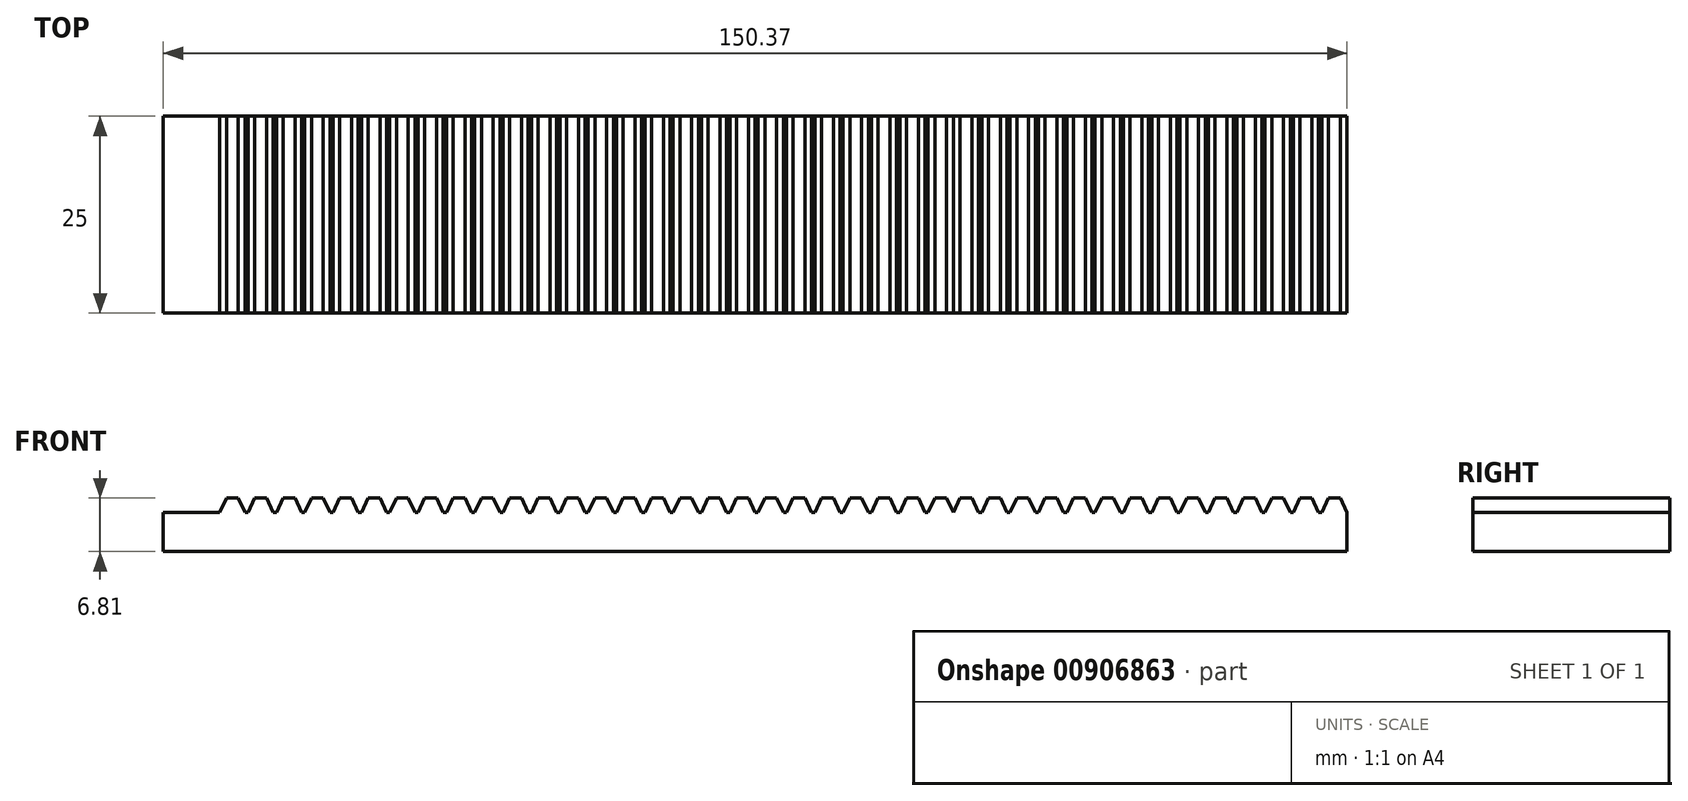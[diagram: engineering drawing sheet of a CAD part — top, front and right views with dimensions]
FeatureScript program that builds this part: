
annotation { "Feature Type Name" : "Feature", "Feature Type Description" : "" }
export const myFeature = defineFeature(function(context is Context, id is Id, definition is map)
    precondition{}
    {
        {
            var Q0;
            Q0=qCreatedBy(makeId("Front.planeOp"),FACE);
            var sketch = newSketch(context, id + "F0", { "sketchPlane" : qUnion([Q0])});
            skLineSegment(sketch, "E0.bottom", {"start": v(0, 5) * mm, "end": v(49.96, 5) * mm});
            skLineSegment(sketch, "E0.top", {"start": v(0, 0) * mm, "end": v(49.96, 0) * mm});
            skLineSegment(sketch, "E1", {"start": v(-4.28, 8.32) * mm, "end": v(-4.28, 8.32) * mm});
            skLineSegment(sketch, "E2", {"start": v(21.59, 5) * mm, "end": v(22.43, 6.81) * mm});
            skLineSegment(sketch, "E3", {"start": v(22.43, 6.81) * mm, "end": v(23.93, 6.81) * mm});
            skLineSegment(sketch, "E4", {"start": v(23.93, 6.81) * mm, "end": v(24.78, 5) * mm});
            skLineSegment(sketch, "E5", {"start": v(-1.09, 8.32) * mm, "end": v(-1.09, 8.32) * mm});
            skLineSegment(sketch, "E6", {"start": v(23.93, 6.81) * mm, "end": v(23.93, -3.78) * mm, "construction": true});
            skLineSegment(sketch, "E7", {"start": v(22.43, 6.81) * mm, "end": v(22.43, -3.82) * mm, "construction": true});
            skLineSegment(sketch, "E8.MirrorCS", {"start": v(26.03, 6.81) * mm, "end": v(25.19, 5) * mm});
            skLineSegment(sketch, "E9.MirrorCS", {"start": v(-0.68, 8.32) * mm, "end": v(-0.68, 8.32) * mm});
            skLineSegment(sketch, "E10.MirrorCS", {"start": v(2.51, 8.32) * mm, "end": v(2.51, 8.32) * mm});
            skLineSegment(sketch, "E11.MirrorCS", {"start": v(27.53, 6.81) * mm, "end": v(26.03, 6.81) * mm});
            skLineSegment(sketch, "E12.MirrorCS", {"start": v(28.38, 5) * mm, "end": v(27.53, 6.81) * mm});
            skLineSegment(sketch, "E13.1.0.0", {"start": v(31.13, 6.81) * mm, "end": v(31.97, 5) * mm});
            skLineSegment(sketch, "E13.1.0.1", {"start": v(28.78, 5) * mm, "end": v(29.63, 6.81) * mm});
            skLineSegment(sketch, "E13.1.0.2", {"start": v(33.23, 6.81) * mm, "end": v(32.38, 5) * mm});
            skLineSegment(sketch, "E13.1.0.3", {"start": v(34.73, 6.81) * mm, "end": v(33.23, 6.81) * mm});
            skLineSegment(sketch, "E13.1.0.4", {"start": v(35.57, 5) * mm, "end": v(34.73, 6.81) * mm});
            skLineSegment(sketch, "E13.1.0.5", {"start": v(29.63, 6.81) * mm, "end": v(31.13, 6.81) * mm});
            skLineSegment(sketch, "E13.2.0.0", {"start": v(38.33, 6.81) * mm, "end": v(39.17, 5) * mm});
            skLineSegment(sketch, "E13.2.0.1", {"start": v(35.98, 5) * mm, "end": v(36.83, 6.81) * mm});
            skLineSegment(sketch, "E13.2.0.5", {"start": v(36.83, 6.81) * mm, "end": v(38.33, 6.81) * mm});
            skLineSegment(sketch, "E13.direction1", {"start": v(21.59, 5) * mm, "end": v(28.78, 5) * mm, "construction": true});
            skLineSegment(sketch, "E14", {"start": v(10.8, 5) * mm, "end": v(11.64, 6.81) * mm});
            skLineSegment(sketch, "E15", {"start": v(11.64, 6.81) * mm, "end": v(13.14, 6.81) * mm});
            skLineSegment(sketch, "E16", {"start": v(13.14, 6.81) * mm, "end": v(13.98, 5) * mm});
            skLineSegment(sketch, "E17", {"start": v(17.99, 5) * mm, "end": v(18.84, 6.81) * mm});
            skLineSegment(sketch, "E18", {"start": v(18.84, 6.81) * mm, "end": v(20.34, 6.81) * mm});
            skLineSegment(sketch, "E19", {"start": v(20.34, 6.81) * mm, "end": v(21.18, 5) * mm});
            skLineSegment(sketch, "E20", {"start": v(14.4, 5) * mm, "end": v(15.24, 6.81) * mm});
            skLineSegment(sketch, "E21", {"start": v(15.24, 6.81) * mm, "end": v(16.74, 6.81) * mm});
            skLineSegment(sketch, "E22", {"start": v(16.74, 6.81) * mm, "end": v(17.58, 5) * mm});
            skLineSegment(sketch, "E23", {"start": v(-4.21, 6.19) * mm, "end": v(53.42, 6.19) * mm, "construction": true});
            skPoint(sketch, "E24", {"position": v(27.82, 6.19) * mm});
            skLineSegment(sketch, "E25", {"start": v(7.2, 5) * mm, "end": v(8.04, 6.81) * mm});
            skLineSegment(sketch, "E26", {"start": v(8.04, 6.81) * mm, "end": v(9.54, 6.81) * mm});
            skLineSegment(sketch, "E27", {"start": v(9.54, 6.81) * mm, "end": v(10.39, 5) * mm});
            skLineSegment(sketch, "E28", {"start": v(3.6, 5) * mm, "end": v(4.44, 6.81) * mm});
            skLineSegment(sketch, "E29", {"start": v(4.44, 6.81) * mm, "end": v(5.94, 6.81) * mm});
            skLineSegment(sketch, "E30", {"start": v(5.94, 6.81) * mm, "end": v(6.79, 5) * mm});
            skLineSegment(sketch, "E31", {"start": v(0, 5) * mm, "end": v(0.85, 6.81) * mm});
            skLineSegment(sketch, "E32", {"start": v(0.85, 6.81) * mm, "end": v(2.35, 6.81) * mm});
            skLineSegment(sketch, "E33", {"start": v(2.35, 6.81) * mm, "end": v(3.2, 5) * mm});
            skLineSegment(sketch, "E34", {"start": v(17.86, 9.76) * mm, "end": v(17.86, 9.76) * mm});
            skLineSegment(sketch, "E35", {"start": v(43.18, 5) * mm, "end": v(44.02, 6.81) * mm});
            skLineSegment(sketch, "E36", {"start": v(44.02, 6.81) * mm, "end": v(45.52, 6.81) * mm});
            skLineSegment(sketch, "E37", {"start": v(45.52, 6.81) * mm, "end": v(46.37, 5) * mm});
            skLineSegment(sketch, "E38", {"start": v(46.77, 5) * mm, "end": v(47.62, 6.81) * mm});
            skLineSegment(sketch, "E39", {"start": v(47.62, 6.81) * mm, "end": v(49.12, 6.81) * mm});
            skLineSegment(sketch, "E40", {"start": v(49.12, 6.81) * mm, "end": v(49.96, 5) * mm});
            skLineSegment(sketch, "E41", {"start": v(16.5, 8.14) * mm, "end": v(16.5, 8.14) * mm});
            skLineSegment(sketch, "E42", {"start": v(39.58, 5) * mm, "end": v(40.42, 6.81) * mm});
            skLineSegment(sketch, "E43", {"start": v(40.42, 6.81) * mm, "end": v(41.92, 6.81) * mm});
            skLineSegment(sketch, "E44", {"start": v(41.92, 6.81) * mm, "end": v(42.77, 5) * mm});
            skLineSegment(sketch, "E45", {"start": v(19.69, 8.14) * mm, "end": v(19.69, 8.14) * mm});
            skLineSegment(sketch, "E46", {"start": v(0, 5) * mm, "end": v(0, 0) * mm});
            skPoint(sketch, "E47.orphan", {"position": v(0, -0.17) * mm});
            skLineSegment(sketch, "E48", {"start": v(49.96, 5) * mm, "end": v(50.37, 5) * mm});
            skLineSegment(sketch, "E49", {"start": v(50.37, 0) * mm, "end": v(49.96, 0) * mm});
            skLineSegment(sketch, "E50.bottom", {"start": v(50.37, 5) * mm, "end": v(100.37, 5) * mm});
            skLineSegment(sketch, "E50.top", {"start": v(50.37, 0) * mm, "end": v(100.37, 0) * mm});
            skLineSegment(sketch, "E51", {"start": v(20.56, -3.86) * mm, "end": v(20.56, -3.86) * mm});
            skLineSegment(sketch, "E52", {"start": v(71.98, 5) * mm, "end": v(72.82, 6.81) * mm});
            skLineSegment(sketch, "E53", {"start": v(72.82, 6.81) * mm, "end": v(74.32, 6.81) * mm});
            skLineSegment(sketch, "E54", {"start": v(74.32, 6.81) * mm, "end": v(75.17, 5) * mm});
            skLineSegment(sketch, "E55", {"start": v(23.75, -3.86) * mm, "end": v(23.75, -3.86) * mm});
            skLineSegment(sketch, "E56", {"start": v(74.32, 6.81) * mm, "end": v(74.32, -3.78) * mm, "construction": true});
            skLineSegment(sketch, "E57", {"start": v(72.82, 6.81) * mm, "end": v(72.82, -3.82) * mm, "construction": true});
            skLineSegment(sketch, "E58.MirrorCS", {"start": v(76.42, 6.81) * mm, "end": v(75.58, 5) * mm});
            skLineSegment(sketch, "E59.MirrorCS", {"start": v(24.16, -3.86) * mm, "end": v(24.16, -3.86) * mm});
            skLineSegment(sketch, "E60.MirrorCS", {"start": v(27.35, -3.86) * mm, "end": v(27.35, -3.86) * mm});
            skLineSegment(sketch, "E61.MirrorCS", {"start": v(77.92, 6.81) * mm, "end": v(76.42, 6.81) * mm});
            skLineSegment(sketch, "E62.MirrorCS", {"start": v(78.77, 5) * mm, "end": v(77.92, 6.81) * mm});
            skLineSegment(sketch, "E63", {"start": v(50.22, 5) * mm, "end": v(100.66, 5) * mm, "construction": true});
            skLineSegment(sketch, "E64.1.0.0", {"start": v(81.52, 6.81) * mm, "end": v(82.36, 5) * mm});
            skLineSegment(sketch, "E64.1.0.1", {"start": v(79.17, 5) * mm, "end": v(80.02, 6.81) * mm});
            skLineSegment(sketch, "E64.1.0.2", {"start": v(83.62, 6.81) * mm, "end": v(82.77, 5) * mm});
            skLineSegment(sketch, "E64.1.0.3", {"start": v(85.12, 6.81) * mm, "end": v(83.62, 6.81) * mm});
            skLineSegment(sketch, "E64.1.0.4", {"start": v(85.96, 5) * mm, "end": v(85.12, 6.81) * mm});
            skLineSegment(sketch, "E64.1.0.5", {"start": v(80.02, 6.81) * mm, "end": v(81.52, 6.81) * mm});
            skLineSegment(sketch, "E64.2.0.0", {"start": v(88.71, 6.81) * mm, "end": v(89.56, 5) * mm});
            skLineSegment(sketch, "E64.2.0.1", {"start": v(86.37, 5) * mm, "end": v(87.21, 6.81) * mm});
            skLineSegment(sketch, "E64.2.0.5", {"start": v(87.21, 6.81) * mm, "end": v(88.71, 6.81) * mm});
            skLineSegment(sketch, "E64.direction1", {"start": v(71.98, 5) * mm, "end": v(79.17, 5) * mm, "construction": true});
            skLineSegment(sketch, "E65", {"start": v(61.18, 5) * mm, "end": v(62.03, 6.81) * mm});
            skLineSegment(sketch, "E66", {"start": v(62.03, 6.81) * mm, "end": v(63.53, 6.81) * mm});
            skLineSegment(sketch, "E67", {"start": v(63.53, 6.81) * mm, "end": v(64.37, 5) * mm});
            skLineSegment(sketch, "E68", {"start": v(68.38, 5) * mm, "end": v(69.22, 6.81) * mm});
            skLineSegment(sketch, "E69", {"start": v(69.22, 6.81) * mm, "end": v(70.72, 6.81) * mm});
            skLineSegment(sketch, "E70", {"start": v(70.72, 6.81) * mm, "end": v(71.57, 5) * mm});
            skLineSegment(sketch, "E71", {"start": v(64.78, 5) * mm, "end": v(65.63, 6.81) * mm});
            skLineSegment(sketch, "E72", {"start": v(65.63, 6.81) * mm, "end": v(67.13, 6.81) * mm});
            skLineSegment(sketch, "E73", {"start": v(67.13, 6.81) * mm, "end": v(67.97, 5) * mm});
            skLineSegment(sketch, "E74", {"start": v(46.18, 6.19) * mm, "end": v(103.81, 6.19) * mm, "construction": true});
            skPoint(sketch, "E75", {"position": v(78.21, 6.19) * mm});
            skLineSegment(sketch, "E76", {"start": v(57.59, 5) * mm, "end": v(58.43, 6.81) * mm});
            skLineSegment(sketch, "E77", {"start": v(58.43, 6.81) * mm, "end": v(59.93, 6.81) * mm});
            skLineSegment(sketch, "E78", {"start": v(59.93, 6.81) * mm, "end": v(60.78, 5) * mm});
            skLineSegment(sketch, "E79", {"start": v(53.99, 5) * mm, "end": v(54.83, 6.81) * mm});
            skLineSegment(sketch, "E80", {"start": v(54.83, 6.81) * mm, "end": v(56.33, 6.81) * mm});
            skLineSegment(sketch, "E81", {"start": v(56.33, 6.81) * mm, "end": v(57.18, 5) * mm});
            skLineSegment(sketch, "E82", {"start": v(50.39, 5) * mm, "end": v(51.23, 6.81) * mm});
            skLineSegment(sketch, "E83", {"start": v(51.23, 6.81) * mm, "end": v(52.73, 6.81) * mm});
            skLineSegment(sketch, "E84", {"start": v(52.73, 6.81) * mm, "end": v(53.58, 5) * mm});
            skLineSegment(sketch, "E85", {"start": v(42.7, -2.42) * mm, "end": v(42.7, -2.42) * mm});
            skLineSegment(sketch, "E86", {"start": v(93.57, 5) * mm, "end": v(94.41, 6.81) * mm});
            skLineSegment(sketch, "E87", {"start": v(94.41, 6.81) * mm, "end": v(95.91, 6.81) * mm});
            skLineSegment(sketch, "E88", {"start": v(95.91, 6.81) * mm, "end": v(96.76, 5) * mm});
            skLineSegment(sketch, "E89", {"start": v(97.16, 5) * mm, "end": v(98, 6.81) * mm});
            skLineSegment(sketch, "E90", {"start": v(98, 6.81) * mm, "end": v(99.5, 6.81) * mm});
            skLineSegment(sketch, "E91", {"start": v(99.5, 6.81) * mm, "end": v(100.35, 5) * mm});
            skLineSegment(sketch, "E92", {"start": v(41.33, -4.04) * mm, "end": v(41.33, -4.04) * mm});
            skLineSegment(sketch, "E93", {"start": v(89.97, 5) * mm, "end": v(90.81, 6.81) * mm});
            skLineSegment(sketch, "E94", {"start": v(90.81, 6.81) * mm, "end": v(92.31, 6.81) * mm});
            skLineSegment(sketch, "E95", {"start": v(92.31, 6.81) * mm, "end": v(93.16, 5) * mm});
            skLineSegment(sketch, "E96", {"start": v(44.52, -4.04) * mm, "end": v(44.52, -4.04) * mm});
            skLineSegment(sketch, "E97.bottom", {"start": v(100.37, 5) * mm, "end": v(150.37, 5) * mm});
            skLineSegment(sketch, "E97.top", {"start": v(100.37, 0) * mm, "end": v(150.37, 0) * mm});
            skLineSegment(sketch, "E97.right", {"start": v(150.37, 5) * mm, "end": v(150.37, 0) * mm});
            skLineSegment(sketch, "E98", {"start": v(120.1, 1.73) * mm, "end": v(120.1, 1.73) * mm});
            skLineSegment(sketch, "E99", {"start": v(121.98, 5) * mm, "end": v(122.82, 6.81) * mm});
            skLineSegment(sketch, "E100", {"start": v(122.82, 6.81) * mm, "end": v(124.32, 6.81) * mm});
            skLineSegment(sketch, "E101", {"start": v(124.32, 6.81) * mm, "end": v(125.17, 5) * mm});
            skLineSegment(sketch, "E102", {"start": v(123.3, 1.73) * mm, "end": v(123.3, 1.73) * mm});
            skLineSegment(sketch, "E103", {"start": v(124.32, 6.81) * mm, "end": v(124.32, -3.78) * mm, "construction": true});
            skLineSegment(sketch, "E104", {"start": v(122.82, 6.81) * mm, "end": v(122.82, -3.82) * mm, "construction": true});
            skLineSegment(sketch, "E105.MirrorCS", {"start": v(126.42, 6.81) * mm, "end": v(125.58, 5) * mm});
            skLineSegment(sketch, "E106.MirrorCS", {"start": v(123.7, 1.73) * mm, "end": v(123.7, 1.73) * mm});
            skLineSegment(sketch, "E107.MirrorCS", {"start": v(126.9, 1.73) * mm, "end": v(126.9, 1.73) * mm});
            skLineSegment(sketch, "E108.MirrorCS", {"start": v(127.92, 6.81) * mm, "end": v(126.42, 6.81) * mm});
            skLineSegment(sketch, "E109.MirrorCS", {"start": v(128.77, 5) * mm, "end": v(127.92, 6.81) * mm});
            skLineSegment(sketch, "E110", {"start": v(100.22, 5) * mm, "end": v(150.66, 5) * mm, "construction": true});
            skLineSegment(sketch, "E111.1.0.0", {"start": v(131.52, 6.81) * mm, "end": v(132.36, 5) * mm});
            skLineSegment(sketch, "E111.1.0.1", {"start": v(129.17, 5) * mm, "end": v(130.02, 6.81) * mm});
            skLineSegment(sketch, "E111.1.0.2", {"start": v(133.62, 6.81) * mm, "end": v(132.77, 5) * mm});
            skLineSegment(sketch, "E111.1.0.3", {"start": v(135.12, 6.81) * mm, "end": v(133.62, 6.81) * mm});
            skLineSegment(sketch, "E111.1.0.4", {"start": v(135.96, 5) * mm, "end": v(135.12, 6.81) * mm});
            skLineSegment(sketch, "E111.1.0.5", {"start": v(130.02, 6.81) * mm, "end": v(131.52, 6.81) * mm});
            skLineSegment(sketch, "E111.2.0.0", {"start": v(138.71, 6.81) * mm, "end": v(139.56, 5) * mm});
            skLineSegment(sketch, "E111.2.0.1", {"start": v(136.37, 5) * mm, "end": v(137.21, 6.81) * mm});
            skLineSegment(sketch, "E111.2.0.5", {"start": v(137.21, 6.81) * mm, "end": v(138.71, 6.81) * mm});
            skLineSegment(sketch, "E111.direction1", {"start": v(121.98, 5) * mm, "end": v(129.17, 5) * mm, "construction": true});
            skLineSegment(sketch, "E112", {"start": v(111.18, 5) * mm, "end": v(112.03, 6.81) * mm});
            skLineSegment(sketch, "E113", {"start": v(112.03, 6.81) * mm, "end": v(113.53, 6.81) * mm});
            skLineSegment(sketch, "E114", {"start": v(113.53, 6.81) * mm, "end": v(114.37, 5) * mm});
            skLineSegment(sketch, "E115", {"start": v(118.38, 5) * mm, "end": v(119.22, 6.81) * mm});
            skLineSegment(sketch, "E116", {"start": v(119.22, 6.81) * mm, "end": v(120.72, 6.81) * mm});
            skLineSegment(sketch, "E117", {"start": v(120.72, 6.81) * mm, "end": v(121.57, 5) * mm});
            skLineSegment(sketch, "E118", {"start": v(114.78, 5) * mm, "end": v(115.63, 6.81) * mm});
            skLineSegment(sketch, "E119", {"start": v(115.63, 6.81) * mm, "end": v(117.13, 6.81) * mm});
            skLineSegment(sketch, "E120", {"start": v(117.13, 6.81) * mm, "end": v(117.97, 5) * mm});
            skLineSegment(sketch, "E121", {"start": v(96.18, 6.19) * mm, "end": v(153.81, 6.19) * mm, "construction": true});
            skPoint(sketch, "E122", {"position": v(128.21, 6.19) * mm});
            skLineSegment(sketch, "E123", {"start": v(107.59, 5) * mm, "end": v(108.43, 6.81) * mm});
            skLineSegment(sketch, "E124", {"start": v(108.43, 6.81) * mm, "end": v(109.93, 6.81) * mm});
            skLineSegment(sketch, "E125", {"start": v(109.93, 6.81) * mm, "end": v(110.78, 5) * mm});
            skLineSegment(sketch, "E126", {"start": v(103.99, 5) * mm, "end": v(104.83, 6.81) * mm});
            skLineSegment(sketch, "E127", {"start": v(104.83, 6.81) * mm, "end": v(106.33, 6.81) * mm});
            skLineSegment(sketch, "E128", {"start": v(106.33, 6.81) * mm, "end": v(107.18, 5) * mm});
            skLineSegment(sketch, "E129", {"start": v(100.39, 5) * mm, "end": v(101.23, 6.81) * mm});
            skLineSegment(sketch, "E130", {"start": v(101.23, 6.81) * mm, "end": v(102.73, 6.81) * mm});
            skLineSegment(sketch, "E131", {"start": v(102.73, 6.81) * mm, "end": v(103.58, 5) * mm});
            skLineSegment(sketch, "E132", {"start": v(142.24, 3.17) * mm, "end": v(142.24, 3.17) * mm});
            skLineSegment(sketch, "E133", {"start": v(143.57, 5) * mm, "end": v(144.41, 6.81) * mm});
            skLineSegment(sketch, "E134", {"start": v(144.41, 6.81) * mm, "end": v(145.91, 6.81) * mm});
            skLineSegment(sketch, "E135", {"start": v(145.91, 6.81) * mm, "end": v(146.76, 5) * mm});
            skLineSegment(sketch, "E136", {"start": v(147.16, 5) * mm, "end": v(148, 6.81) * mm});
            skLineSegment(sketch, "E137", {"start": v(148, 6.81) * mm, "end": v(149.5, 6.81) * mm});
            skLineSegment(sketch, "E138", {"start": v(149.5, 6.81) * mm, "end": v(150.35, 5) * mm});
            skLineSegment(sketch, "E139", {"start": v(140.88, 1.56) * mm, "end": v(140.88, 1.56) * mm});
            skLineSegment(sketch, "E140", {"start": v(139.97, 5) * mm, "end": v(140.81, 6.81) * mm});
            skLineSegment(sketch, "E141", {"start": v(140.81, 6.81) * mm, "end": v(142.31, 6.81) * mm});
            skLineSegment(sketch, "E142", {"start": v(142.31, 6.81) * mm, "end": v(143.16, 5) * mm});
            skLineSegment(sketch, "E143", {"start": v(144.07, 1.56) * mm, "end": v(144.07, 1.56) * mm});
            skSolve(sketch);
        }
        {
            var Q0;
            Q0 = qSketchRegion(id + "F0", true);
            extrude(context, id + "F1", {"entities" : qUnion([Q0]), "depth" : 25 * mm, "offsetDistance" : 25 * mm});
        }
    });
